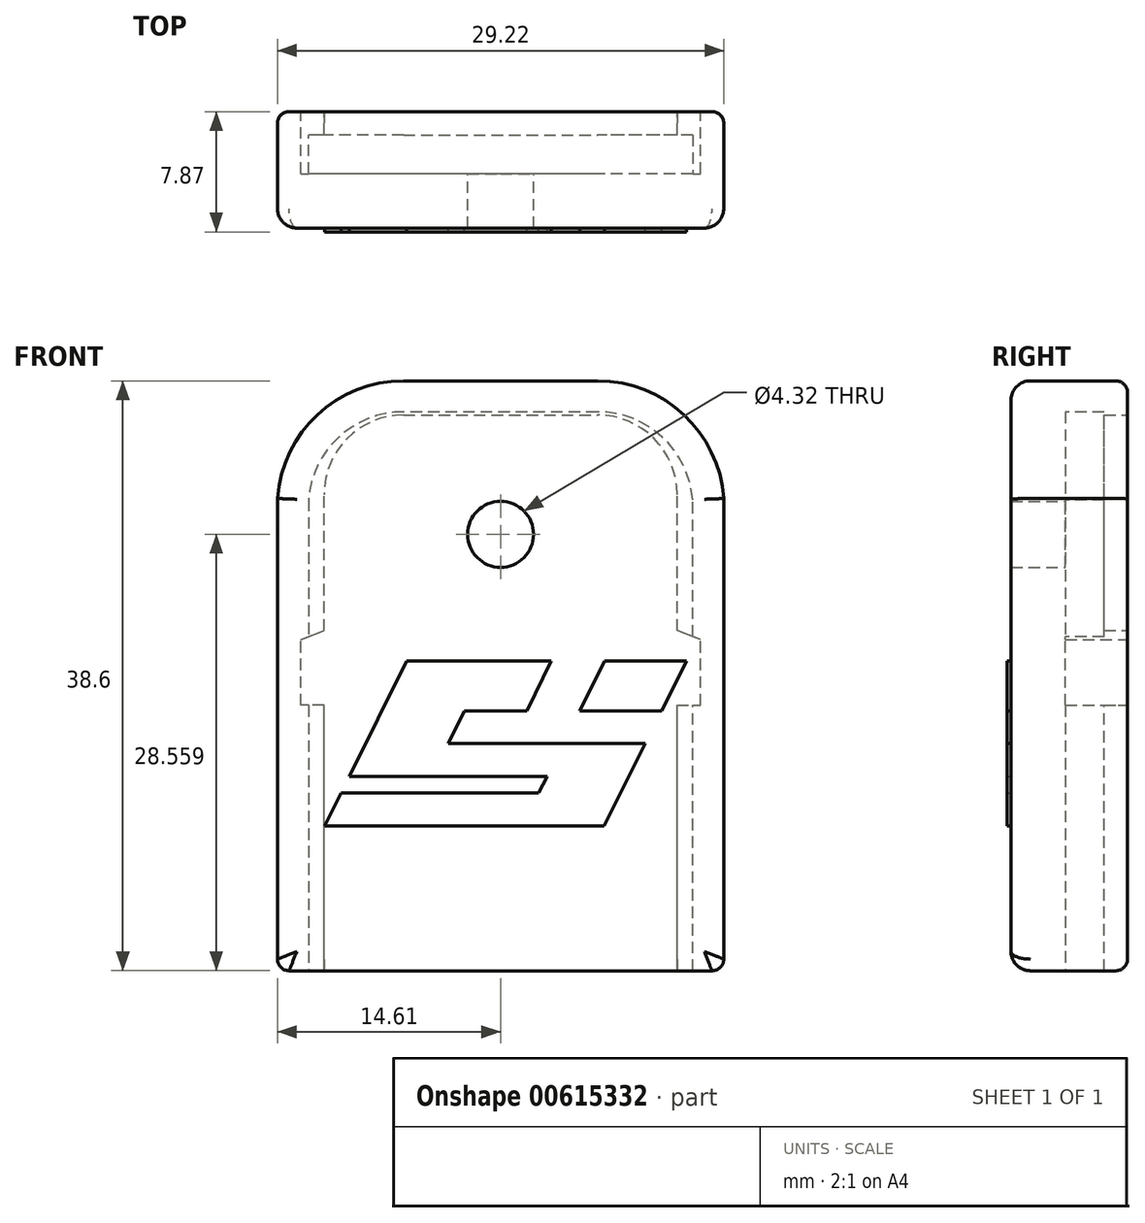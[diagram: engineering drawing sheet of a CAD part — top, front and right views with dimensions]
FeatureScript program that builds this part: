
annotation { "Feature Type Name" : "Feature", "Feature Type Description" : "" }
export const myFeature = defineFeature(function(context is Context, id is Id, definition is map)
    precondition{}
    {
        {
            var Q0;
            Q0=qCreatedBy(makeId("Front.planeOp"),FACE);
            var sketch = newSketch(context, id + "F0", { "sketchPlane" : qUnion([Q0])});
            skLineSegment(sketch, "E0.bottom", {"start": v(14.6, 19.3) * mm, "end": v(-14.6, 19.3) * mm});
            skLineSegment(sketch, "E0.top", {"start": v(14.6, -19.3) * mm, "end": v(-14.6, -19.3) * mm});
            skLineSegment(sketch, "E0.left", {"start": v(14.6, 19.3) * mm, "end": v(14.6, -19.3) * mm});
            skLineSegment(sketch, "E0.right", {"start": v(-14.6, 19.3) * mm, "end": v(-14.6, -19.3) * mm});
            skPoint(sketch, "E0.middle", {"position": v(0, 0) * mm});
            skPoint(sketch, "E1.endSnap0", {"position": v(0, 19.3) * mm});
            skLineSegment(sketch, "E2", {"start": v(0, 19.3) * mm, "end": v(6.35, 19.3) * mm, "construction": true});
            skLineSegment(sketch, "E3", {"start": v(0, 26.8) * mm, "end": v(0, -22.8) * mm, "construction": true});
            skPoint(sketch, "E3.endSnap0", {"position": v(0, -19.3) * mm});
            skLineSegment(sketch, "E4.MirrorCS", {"start": v(0, 19.3) * mm, "end": v(-6.35, 19.3) * mm, "construction": true});
            skArc(sketch, "E5", {"start": v(-6.35, 19.3) * mm, "mid": v(-12.4, 16.68) * mm, "end": v(-14.6, 10.46) * mm});
            skArc(sketch, "E6.MirrorCS", {"start": v(6.35, 19.3) * mm, "mid": v(12.4, 16.68) * mm, "end": v(14.6, 10.46) * mm});
            skSolve(sketch);
        }
        {
            var Q0;
            {var subQ4=sQuery(id+"F0.wireOp",EDGE,"E0.top");Q0=makeQuery(id+"F0.imprint","IMPRINT",FACE,{"disambiguationData":[TD([[makeQuery(id+"F0.imprint","IMPRINT",EDGE,{"derivedFrom":subQ4}),-1.0]])]});}
            extrude(context, id + "F1", {"entities" : qUnion([Q0]), "depth" : 7.62 * mm, "offsetDistance" : 25.4 * mm});
        }
        {
            var Q0;
            Q0=qCreatedBy(makeId("Front.planeOp"),FACE);
            var sketch = newSketch(context, id + "F2", { "sketchPlane" : qUnion([Q0])});
            skLineSegment(sketch, "E7", {"start": v(0, 19.42) * mm, "end": v(0, 9.26) * mm, "construction": true});
            skCircle(sketch, "E8", {"center": v(0, 9.26) * mm, "radius": 2.16 * mm});
            skSolve(sketch);
        }
        {
            var Q0;
            Q0 = qSketchRegion(id + "F2", true);
            extrude(context, id + "F3", {"entities" : qUnion([Q0]), "operationType" : NewBodyOperationType.REMOVE, "depth" : 25.4 * mm, "offsetDistance" : 25.4 * mm});
        }
        {
            var Q0;
            Q0=qCreatedBy(makeId("Front.planeOp"),FACE);
            var sketch = newSketch(context, id + "F4", { "sketchPlane" : qUnion([Q0])});
            skLineSegment(sketch, "E9.bottom", {"start": v(11.56, -22.18) * mm, "end": v(-11.56, -22.18) * mm});
            skLineSegment(sketch, "E9.left", {"start": v(11.56, -22.18) * mm, "end": v(11.56, -1.93) * mm});
            skLineSegment(sketch, "E9.right", {"start": v(-11.56, -22.18) * mm, "end": v(-11.56, -1.93) * mm});
            skPoint(sketch, "E9.middle", {"position": v(0, 0) * mm});
            skLineSegment(sketch, "E10", {"start": v(5.3, 17.06) * mm, "end": v(-6.35, 17.06) * mm});
            skLineSegment(sketch, "E11", {"start": v(-6.35, 17.06) * mm, "end": v(6.35, 17.06) * mm});
            skPoint(sketch, "E12.orphan", {"position": v(11.56, 22.18) * mm});
            skPoint(sketch, "E13.orphan", {"position": v(-11.56, 22.18) * mm});
            skLineSegment(sketch, "E14", {"start": v(0, 17.06) * mm, "end": v(6.35, 17.06) * mm, "construction": true});
            skLineSegment(sketch, "E15.MirrorCS", {"start": v(0, 17.06) * mm, "end": v(-6.35, 17.06) * mm, "construction": true});
            skArc(sketch, "E16", {"start": v(11.56, 11.86) * mm, "mid": v(10.03, 15.54) * mm, "end": v(6.35, 17.06) * mm});
            skArc(sketch, "E17.MirrorCS", {"start": v(-11.56, 11.86) * mm, "mid": v(-10.03, 15.54) * mm, "end": v(-6.35, 17.06) * mm});
            skPoint(sketch, "E18.orphan", {"position": v(11.56, 17.06) * mm});
            skPoint(sketch, "E19.orphan", {"position": v(-11.56, 17.06) * mm});
            skLineSegment(sketch, "E20", {"start": v(-11.56, -1.93) * mm, "end": v(-13.08, -1.93) * mm});
            skLineSegment(sketch, "E21", {"start": v(-13.08, -1.93) * mm, "end": v(-13.08, 2.37) * mm});
            skLineSegment(sketch, "E22", {"start": v(-13.08, 2.37) * mm, "end": v(-11.56, 2.96) * mm});
            skLineSegment(sketch, "E23.MirrorCS", {"start": v(13.08, 2.37) * mm, "end": v(11.56, 2.96) * mm});
            skLineSegment(sketch, "E24.MirrorCS", {"start": v(13.08, -1.93) * mm, "end": v(13.08, 2.37) * mm});
            skLineSegment(sketch, "E25.MirrorCS", {"start": v(11.56, -1.93) * mm, "end": v(13.08, -1.93) * mm});
            skLineSegment(sketch, "E26.trimOffspring", {"start": v(-11.56, 2.96) * mm, "end": v(-11.56, 11.86) * mm});
            skLineSegment(sketch, "E27.trimOffspring", {"start": v(11.56, 2.96) * mm, "end": v(11.56, 11.86) * mm});
            skSolve(sketch);
        }
        {
            var Q0;
            Q0 = qSketchRegion(id + "F4", true);
            extrude(context, id + "F5", {"entities" : qUnion([Q0]), "operationType" : NewBodyOperationType.REMOVE, "depth" : 4.06 * mm, "offsetDistance" : 25.4 * mm});
        }
        {
            var Q0;
            Q0=qCreatedBy(makeId("Top.planeOp"),FACE);
            var sketch = newSketch(context, id + "F6", { "sketchPlane" : qUnion([Q0])});
            skLineSegment(sketch, "E28.bottom", {"start": v(-12.57, -4.08) * mm, "end": v(12.57, -4.08) * mm});
            skLineSegment(sketch, "E28.top", {"start": v(-12.57, -1.54) * mm, "end": v(12.57, -1.54) * mm});
            skLineSegment(sketch, "E28.left", {"start": v(-12.57, -4.08) * mm, "end": v(-12.57, -1.54) * mm});
            skLineSegment(sketch, "E28.right", {"start": v(12.57, -4.08) * mm, "end": v(12.57, -1.54) * mm});
            skPoint(sketch, "E28.middle", {"position": v(0, -2.8) * mm});
            skSolve(sketch);
        }
        {
            var Q0;
            Q0=makeQuery(id+"F1.opExtrude","CAP_EDGE",EDGE,{"disambiguationData":[OSD([sQuery(id+"F0.wireOp",EDGE,"E0.left")])],"isStart":false});
            var Q1;
            Q1=makeQuery(id+"F1.opExtrude","CAP_EDGE",EDGE,{"disambiguationData":[OSD([sQuery(id+"F0.wireOp",EDGE,"E6.MirrorCS")])],"isStart":false});
            var Q2;
            Q2=makeQuery(id+"F1.opExtrude","CAP_EDGE",EDGE,{"disambiguationData":[OSD([sQuery(id+"F0.wireOp",EDGE,"E0.bottom")])],"isStart":false});
            var Q3;
            Q3=makeQuery(id+"F1.opExtrude","CAP_EDGE",EDGE,{"disambiguationData":[OSD([sQuery(id+"F0.wireOp",EDGE,"E5")])],"isStart":false});
            var Q4;
            Q4=makeQuery(id+"F1.opExtrude","CAP_EDGE",EDGE,{"disambiguationData":[OSD([sQuery(id+"F0.wireOp",EDGE,"E0.right")])],"isStart":false});
            var Q5;
            Q5=makeQuery(id+"F1.opExtrude","CAP_EDGE",EDGE,{"disambiguationData":[OSD([sQuery(id+"F0.wireOp",EDGE,"E0.top")])],"isStart":false});
            fillet(context, id + "F7", {"entities" : qUnion([Q0, Q1, Q2, Q3, Q4, Q5]), "radius" : 1.27 * mm, "tangentPropagation" : true, "allowEdgeOverflow" : false});
        }
        {
            var Q0;
            Q0=makeQuery(id+"F1.opExtrude","SWEPT_EDGE",EDGE,{"disambiguationData":[OSD([sQuery(id+"F0.wireOp",EDGE,"E0.top"),sQuery(id+"F0.wireOp",EDGE,"E0.left")])]});
            var Q1;
            Q1=makeQuery(id+"F1.opExtrude","SWEPT_EDGE",EDGE,{"disambiguationData":[OSD([sQuery(id+"F0.wireOp",EDGE,"E0.top"),sQuery(id+"F0.wireOp",EDGE,"E0.right")])]});
            fillet(context, id + "F8", {"entities" : qUnion([Q0, Q1]), "radius" : 0.76 * mm, "tangentPropagation" : true, "allowEdgeOverflow" : false});
        }
        {
            var Q0;
            Q0=makeQuery(id+"F1.opExtrude","CAP_EDGE",EDGE,{"disambiguationData":[OSD([sQuery(id+"F0.wireOp",EDGE,"E0.left")])],"isStart":true});
            var Q1;
            Q1=makeQuery(id+"F1.opExtrude","CAP_EDGE",EDGE,{"disambiguationData":[OSD([sQuery(id+"F0.wireOp",EDGE,"E6.MirrorCS")])],"isStart":true});
            var Q2;
            Q2=makeQuery(id+"F1.opExtrude","CAP_EDGE",EDGE,{"disambiguationData":[OSD([sQuery(id+"F0.wireOp",EDGE,"E0.bottom")])],"isStart":true});
            var Q3;
            Q3=makeQuery(id+"F1.opExtrude","CAP_EDGE",EDGE,{"disambiguationData":[OSD([sQuery(id+"F0.wireOp",EDGE,"E5")])],"isStart":true});
            var Q4;
            Q4=makeQuery(id+"F1.opExtrude","CAP_EDGE",EDGE,{"disambiguationData":[OSD([sQuery(id+"F0.wireOp",EDGE,"E0.right")])],"isStart":true});
            fillet(context, id + "F9", {"entities" : qUnion([Q0, Q1, Q2, Q3, Q4]), "radius" : 0.76 * mm, "tangentPropagation" : true, "allowEdgeOverflow" : false});
        }
        {
            var Q0;
            Q0=makeQuery(id+"F1.opExtrude","CAP_FACE",FACE,{"disambiguationData":[OSD([sQuery(id+"F0.wireOp",EDGE,"E0.bottom"),sQuery(id+"F0.wireOp",EDGE,"E0.top"),sQuery(id+"F0.wireOp",EDGE,"E0.left"),sQuery(id+"F0.wireOp",EDGE,"E0.right"),sQuery(id+"F0.wireOp",EDGE,"E5"),sQuery(id+"F0.wireOp",EDGE,"E6.MirrorCS")])],"isStart":false});
            var sketch = newSketch(context, id + "F10", { "sketchPlane" : qUnion([Q0])});
            skLineSegment(sketch, "E29.0", {"start": v(-12.57, 11.52) * mm, "end": v(-12.57, -18.03) * mm});
            skLineSegment(sketch, "E29.1", {"start": v(12.57, -18.03) * mm, "end": v(12.57, 11.52) * mm});
            skArc(sketch, "E29.2", {"start": v(12.57, 11.52) * mm, "mid": v(10.59, 15.62) * mm, "end": v(6.35, 17.27) * mm});
            skLineSegment(sketch, "E29.3", {"start": v(6.35, 17.27) * mm, "end": v(-6.35, 17.27) * mm});
            skArc(sketch, "E29.4", {"start": v(-6.35, 17.27) * mm, "mid": v(-10.59, 15.62) * mm, "end": v(-12.57, 11.52) * mm});
            skLineSegment(sketch, "E30", {"start": v(12.57, -18.03) * mm, "end": v(12.57, -26.18) * mm});
            skLineSegment(sketch, "E31", {"start": v(12.57, -26.18) * mm, "end": v(-12.57, -26.18) * mm});
            skLineSegment(sketch, "E32", {"start": v(-12.57, -26.18) * mm, "end": v(-12.57, -18.03) * mm});
            skSolve(sketch);
        }
        {
            var Q0;
            {var subQ1=sQuery(id+"F10.wireOp",EDGE,"E29.0");Q0=makeQuery(id+"F10.imprint","IMPRINT",FACE,{"disambiguationData":[TD([[makeQuery(id+"F10.imprint","IMPRINT",EDGE,{"derivedFrom":subQ1}),1.0]])]});}
            var Q1;
            {var subQ0=sQuery(id+"F10.wireOp",EDGE,"E30");Q1=makeQuery(id+"F10.imprint","IMPRINT",FACE,{"disambiguationData":[TD([[makeQuery(id+"F10.imprint","IMPRINT",EDGE,{"derivedFrom":subQ0}),-1.0]])]});}
            extrude(context, id + "F11", {"entities" : qUnion([Q0, Q1]), "operationType" : NewBodyOperationType.REMOVE, "oppositeDirection" : true, "depth" : 6.1 * mm, "offsetDistance" : 25.4 * mm, "hasSecondDirection" : true, "secondDirectionOppositeDirection" : true, "secondDirectionDepth" : 3.56 * mm});
        }
        {
            var Q0;
            Q0=makeQuery(id+"F1.opExtrude","CAP_FACE",FACE,{"disambiguationData":[OSD([sQuery(id+"F0.wireOp",EDGE,"E0.bottom"),sQuery(id+"F0.wireOp",EDGE,"E0.top"),sQuery(id+"F0.wireOp",EDGE,"E0.left"),sQuery(id+"F0.wireOp",EDGE,"E0.right"),sQuery(id+"F0.wireOp",EDGE,"E5"),sQuery(id+"F0.wireOp",EDGE,"E6.MirrorCS")])],"isStart":false});
            var sketch = newSketch(context, id + "F12", { "sketchPlane" : qUnion([Q0])});
            skLineSegment(sketch, "E33", {"start": v(-6.17, 0.97) * mm, "end": v(3.3, 0.97) * mm});
            skLineSegment(sketch, "E34", {"start": v(3.3, 0.97) * mm, "end": v(1.7, -2.32) * mm});
            skLineSegment(sketch, "E35", {"start": v(1.7, -2.32) * mm, "end": v(-2.37, -2.32) * mm});
            skLineSegment(sketch, "E36", {"start": v(-2.37, -2.32) * mm, "end": v(-3.43, -4.44) * mm});
            skLineSegment(sketch, "E37", {"start": v(-3.43, -4.44) * mm, "end": v(9.46, -4.44) * mm});
            skLineSegment(sketch, "E38", {"start": v(9.46, -4.44) * mm, "end": v(6.77, -9.84) * mm});
            skLineSegment(sketch, "E39", {"start": v(6.77, -9.84) * mm, "end": v(-11.53, -9.84) * mm});
            skLineSegment(sketch, "E40", {"start": v(-11.53, -9.84) * mm, "end": v(-10.45, -7.67) * mm});
            skLineSegment(sketch, "E41", {"start": v(-10.45, -7.67) * mm, "end": v(2.48, -7.67) * mm});
            skLineSegment(sketch, "E42", {"start": v(2.48, -7.67) * mm, "end": v(3.04, -6.6) * mm});
            skLineSegment(sketch, "E43", {"start": v(3.04, -6.6) * mm, "end": v(-9.91, -6.6) * mm});
            skLineSegment(sketch, "E44", {"start": v(-9.91, -6.6) * mm, "end": v(-6.17, 0.97) * mm});
            skLineSegment(sketch, "E45", {"start": v(5.17, -2.32) * mm, "end": v(10.54, -2.32) * mm});
            skLineSegment(sketch, "E46", {"start": v(10.54, -2.32) * mm, "end": v(12.17, 0.97) * mm});
            skLineSegment(sketch, "E47", {"start": v(12.17, 0.97) * mm, "end": v(6.8, 0.97) * mm});
            skLineSegment(sketch, "E48", {"start": v(6.8, 0.97) * mm, "end": v(5.17, -2.32) * mm});
            skSolve(sketch);
        }
        {
            var Q0;
            Q0 = qSketchRegion(id + "F12", true);
            extrude(context, id + "F13", {"entities" : qUnion([Q0]), "operationType" : NewBodyOperationType.ADD, "depth" : 0.25 * mm, "offsetDistance" : 25.4 * mm});
        }
    });
